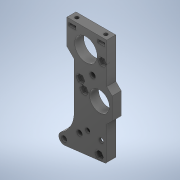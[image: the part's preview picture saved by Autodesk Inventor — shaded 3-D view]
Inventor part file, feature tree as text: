
AUTODESK INVENTOR PART (.ipt)
format: ipt  version: 2020 (Build 240168000, 168)  size: 570,880 bytes
history: native  units: mm
features: extrude x14, sketch x10, fillet x5, projected_geometry x5, thread x2, chamfer x1, mirror x1
ambient origin geometry x8: Origin, YZ Plane, XZ Plane, XY Plane, X Axis, Y Axis, Z Axis, Center Point
bodies: Solid1 (feature_tree)
feature tree (38):
  extrude  "Extrusion1"  Depth=23.5mm
  fillet  "Fillet1"  Radius=23.5mm
  fillet  "Fillet2"  Radius=6.0mm
  extrude  "Extrusion2"  Depth=3.0mm
  extrude  "Extrusion3"  Depth=4.0mm
  thread  "Thread1"  [1 undecoded]
  thread  "Thread2"  [1 undecoded]
  extrude  "Extrusion4"  Depth=24.75mm
  extrude  "Extrusion5"  Depth=2.1mm
  extrude  "Extrusion6"  Depth=4.0mm
  extrude  "Extrusion7"  TaperAngle=45.0deg  [1 undecoded]
  extrude  "Extrusion8"  Depth=12.0mm
  extrude  "Extrusion9"  TaperAngle=135.0deg  [1 undecoded]
  extrude  "Extrusion10"  Depth=5.0mm TaperAngle=0.0deg
  fillet  "Fillet3"  Radius=3.0mm
  extrude  "Extrusion11"  Depth=10.0mm
  chamfer  "Chamfer1"  Distance=3.0mm
  fillet  "Fillet4"  Radius=2.5mm
  extrude  "Extrusion12"  Depth=0.5mm
  extrude  "Extrusion13"  Depth=7.5mm
  extrude  "Extrusion14"  Depth=0.5mm
  fillet  "Fillet5"  Radius=15.0mm
  mirror  "Mirror2"
  sketch  "Sketch3"  dims[d0=3.0mm d1=6.0mm d2=23.5mm d3=6.0mm]
  projected_geometry  "Projected Loop1"
  sketch  "Sketch5"  dims[d4=0.0mm d5=3.0mm]
  sketch  "Sketch7"  dims[d6=18.0mm d7=56.0mm d8=11.0mm d9=4.0mm]
  sketch  "Sketch8"  dims[d10=24.75mm d11=12.5mm]
  projected_geometry  "Projected Loop2"
  sketch  "Sketch10"  dims[d12=22.3mm d14=2.1mm]
  sketch  "Sketch13"  dims[d18=30.0mm d20=360.0deg d22=4.0mm]
  sketch  "Sketch15"  dims[d23=14.0mm d24=45.0deg]
  sketch  "Sketch17"  dims[d25=3.0mm d26=12.0mm]
  projected_geometry  "Projected Loop3"
  sketch  "Sketch21"  dims[d27=6.0mm d28=135.0deg]
  projected_geometry  "Projected Loop5"
  sketch  "Sketch22"  dims[d29=135.0deg d30=5.0mm d31=0.0mm d32=3.0mm d33=10.0mm d34=3.0mm d35=2.5mm d36=13.5mm d37=7.5mm d38=2.5mm d39=15.0mm d40=12.5mm d41=1.0mm d42=15.0mm d43=12.75mm d44=20.0mm d45=23.75mm d46=3.0mm d47=0.0mm d48=2.0mm d49=2.0mm d50=2.5mm d51=2.5mm d52=3.0mm d53=3.0mm d54=4.5mm d55=0.0mm d56=7.0mm d57=0.0mm d58=7.0mm d59=0.0mm d60=8.5mm d61=270.0deg d62=4.0mm d63=4.0mm d64=4.0mm d65=3.0mm d66=0.0mm d67=5.5mm d68=2.0mm d69=0.0mm d70=4.0mm d71=1.85mm d72=4.0mm d73=1.85mm d74=1.0mm d75=2.8mm d76=2.8mm d77=1.0mm d78=10.0mm d79=0.0mm d82=3.1mm d83=11.15mm d84=2.1mm d85=2.1mm d86=2.1mm d87=5.5mm d88=3.5mm d89=25.75mm d90=30.25mm d91=2.5mm d92=11.75mm d93=24.0mm d94=8.0mm d95=2.1mm d96=2.1mm d98=2.1mm d99=1.8mm d100=0.0mm d101=2.1mm d102=2.1mm d103=2.1mm d104=1.8mm d105=0.0mm d117=3.9mm d118=0.0mm d119=18.0mm d120=6.5mm d121=0.0mm d122=1.0mm d125=5.0mm d126=7.25mm d127=2.5mm d128=5.0mm d129=15.0mm d130=5.0mm d131=5.0mm d132=90.0deg d133=135.0deg d135=135.0deg d136=135.0deg d137=3.0mm d138=0.0mm d139=0.9mm d140=2.0mm d141=45.0deg d142=4.0mm d143=2.0mm d144=2.6mm d145=3.625mm d146=10.0mm d147=0.0mm d148=2.05mm d149=2.4mm d150=0.0mm d151=4.5mm d154=1.0mm d155=0.0mm d156=2.0mm d157=2.8mm d80=0.5mm d81=0.872665mm d106=0.872665mm d123=0.872665mm d134=0.5mm d153=0.5mm d158=0.5mm d159=0.872665mm d160=0.5mm d161=0.872665mm]
  projected_geometry  "Projected Loop6"
note: 4 required parameter values undecoded (feature->parameter linkage not recoverable at this tier; creation-order binding heuristic only, values carry confidence <= 0.55)
